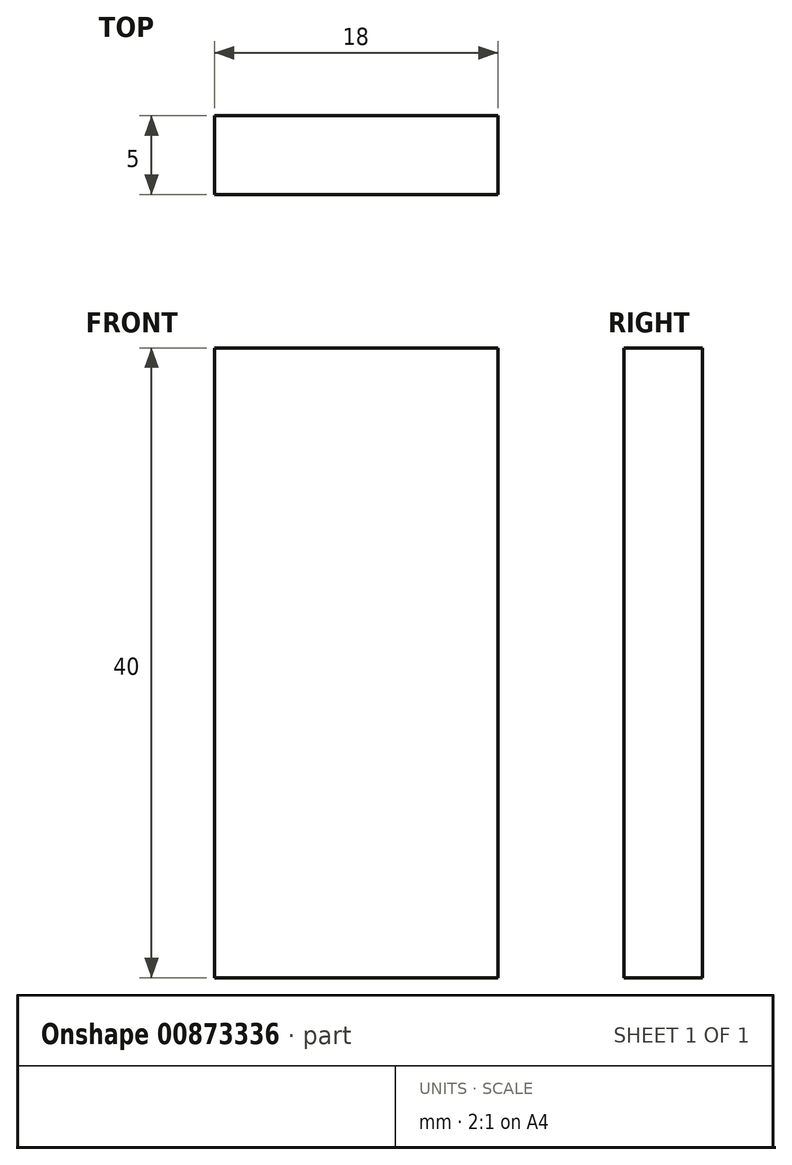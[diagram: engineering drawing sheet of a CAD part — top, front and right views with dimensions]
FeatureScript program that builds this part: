
annotation { "Feature Type Name" : "Feature", "Feature Type Description" : "" }
export const myFeature = defineFeature(function(context is Context, id is Id, definition is map)
    precondition{}
    {
        {
            var Q0;
            Q0=qCreatedBy(makeId("Front.planeOp"),FACE);
            var sketch = newSketch(context, id + "F0", { "sketchPlane" : qUnion([Q0])});
            skLineSegment(sketch, "E0.bottom", {"start": v(0, 0) * mm, "end": v(18, 0) * mm});
            skLineSegment(sketch, "E0.top", {"start": v(0, -40) * mm, "end": v(18, -40) * mm});
            skLineSegment(sketch, "E0.left", {"start": v(0, 0) * mm, "end": v(0, -40) * mm});
            skLineSegment(sketch, "E0.right", {"start": v(18, 0) * mm, "end": v(18, -40) * mm});
            skSolve(sketch);
        }
        {
            var Q0;
            Q0=makeQuery(id+"F0.imprint","IMPRINT",FACE,{"disambiguationData":[TD([[makeQuery(id+"F0.imprint","IMPRINT",EDGE,{"derivedFrom":sQuery(id+"F0.wireOp",EDGE,"E0.bottom")}),-1.0]])]});
            extrude(context, id + "F1", {"entities" : qUnion([Q0]), "depth" : 5 * mm, "offsetDistance" : 25 * mm});
        }
    });
